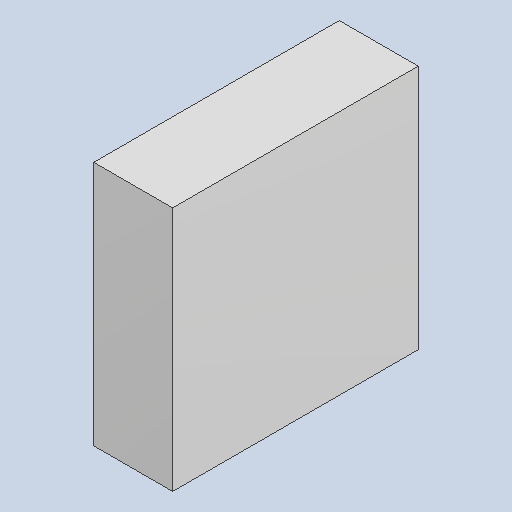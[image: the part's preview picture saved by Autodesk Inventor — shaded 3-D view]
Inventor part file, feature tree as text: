
AUTODESK INVENTOR PART (.ipt)
format: ipt  version: 2023.4 (Build 274418000, 418)  size: 81,408 bytes
history: native  units: mm
features: extrude x1
ambient origin geometry x8: Origin, YZ Plane, XZ Plane, XY Plane, X Axis, Y Axis, Z Axis, Center Point
bodies: Solid1 (feature_tree)
feature tree (1):
  extrude  "Extruded_9"  [1 undecoded]
note: 1 required parameter value undecoded (feature->parameter linkage not recoverable at this tier; creation-order binding heuristic only, values carry confidence <= 0.55)
